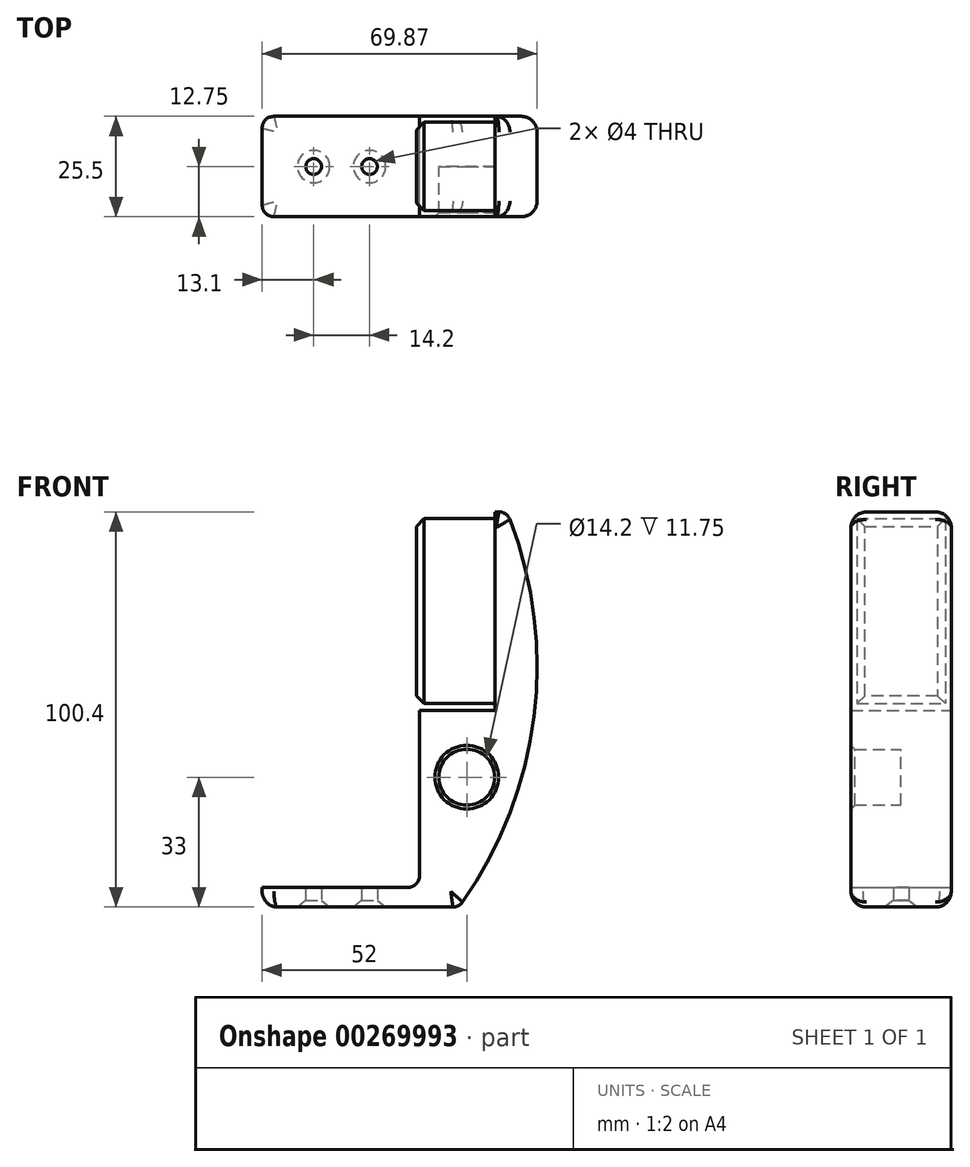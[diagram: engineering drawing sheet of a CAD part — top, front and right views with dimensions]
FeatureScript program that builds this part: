
annotation { "Feature Type Name" : "Feature", "Feature Type Description" : "" }
export const myFeature = defineFeature(function(context is Context, id is Id, definition is map)
    precondition{}
    {
        {
            var Q0;
            Q0=qCreatedBy(makeId("Front.planeOp"),FACE);
            var sketch = newSketch(context, id + "F0", { "sketchPlane" : qUnion([Q0])});
            skLineSegment(sketch, "E0.bottom", {"start": v(0, 0) * mm, "end": v(-40, 0) * mm});
            skLineSegment(sketch, "E0.top", {"start": v(0, 5) * mm, "end": v(-40, 5) * mm});
            skLineSegment(sketch, "E0.right", {"start": v(-40, 0) * mm, "end": v(-40, 5) * mm});
            skLineSegment(sketch, "E1", {"start": v(0, 5) * mm, "end": v(0, 50) * mm});
            skLineSegment(sketch, "E2", {"start": v(0, 50) * mm, "end": v(19.2, 50) * mm});
            skLineSegment(sketch, "E3", {"start": v(19.2, 50) * mm, "end": v(19.2, 51.7) * mm});
            skLineSegment(sketch, "E4", {"start": v(19.2, 51.7) * mm, "end": v(-0.8, 51.7) * mm});
            skLineSegment(sketch, "E5", {"start": v(-0.8, 51.7) * mm, "end": v(-0.8, 98.7) * mm});
            skLineSegment(sketch, "E6", {"start": v(-0.8, 98.7) * mm, "end": v(19.2, 98.7) * mm});
            skLineSegment(sketch, "E7", {"start": v(19.2, 98.7) * mm, "end": v(19.2, 100.4) * mm});
            skLineSegment(sketch, "E8", {"start": v(0, 0) * mm, "end": v(10, 0) * mm});
            skArc(sketch, "E9", {"start": v(10, 0) * mm, "mid": v(29.1, 48.62) * mm, "end": v(22.2, 100.4) * mm});
            skLineSegment(sketch, "E10", {"start": v(19.2, 100.4) * mm, "end": v(22.2, 100.4) * mm});
            skLineSegment(sketch, "E11", {"start": v(19.2, 98.7) * mm, "end": v(19.2, 51.7) * mm});
            skCircle(sketch, "E12", {"center": v(12, 33) * mm, "radius": 7.1 * mm});
            skSolve(sketch);
        }
        {
            var Q0;
            Q0=makeQuery(id+"F0.imprint","IMPRINT",FACE,{"disambiguationData":[TD([[makeQuery(id+"F0.imprint","IMPRINT",EDGE,{"derivedFrom":sQuery(id+"F0.wireOp",EDGE,"E0.bottom")}),-1.0]])]});
            extrude(context, id + "F1", {"entities" : qUnion([Q0]), "depth" : 12.75 * mm, "offsetDistance" : 25 * mm, "hasSecondDirection" : true, "secondDirectionOppositeDirection" : true, "secondDirectionDepth" : 12.75 * mm});
        }
        {
            var Q0;
            Q0=makeQuery(id+"F0.imprint","IMPRINT",FACE,{"disambiguationData":[TD([[makeQuery(id+"F0.imprint","IMPRINT",EDGE,{"derivedFrom":sQuery(id+"F0.wireOp",EDGE,"E4")}),-1.0]])]});
            extrude(context, id + "F2", {"entities" : qUnion([Q0]), "operationType" : NewBodyOperationType.ADD, "depth" : 11.25 * mm, "offsetDistance" : 25 * mm, "hasSecondDirection" : true, "secondDirectionOppositeDirection" : true, "secondDirectionDepth" : 11.25 * mm});
        }
        {
            var Q0;
            Q0=makeQuery(id+"F1.opExtrude","SWEPT_EDGE",EDGE,{"disambiguationData":[OSD([sQuery(id+"F0.wireOp",EDGE,"E0.top"),sQuery(id+"F0.wireOp",EDGE,"E1")])]});
            var Q1;
            Q1=makeQuery(id+"F1.opExtrude","CAP_EDGE",EDGE,{"disambiguationData":[OSD([sQuery(id+"F0.wireOp",EDGE,"E0.right")])],"isStart":false});
            var Q2;
            Q2=makeQuery(id+"F1.opExtrude","CAP_EDGE",EDGE,{"disambiguationData":[OSD([sQuery(id+"F0.wireOp",EDGE,"E0.right")])],"isStart":true});
            var Q3;
            Q3=makeQuery(id+"F1.opExtrude","SWEPT_EDGE",EDGE,{"disambiguationData":[OSD([sQuery(id+"F0.wireOp",EDGE,"E8"),sQuery(id+"F0.wireOp",EDGE,"E9")])]});
            var Q4;
            Q4=makeQuery(id+"F1.opExtrude","SWEPT_EDGE",EDGE,{"disambiguationData":[OSD([sQuery(id+"F0.wireOp",EDGE,"E9"),sQuery(id+"F0.wireOp",EDGE,"E10")])]});
            fillet(context, id + "F3", {"entities" : qUnion([Q0, Q1, Q2, Q3, Q4]), "tangentPropagation" : true, "radius" : 3 * mm, "defaultsChanged" : false, "vertexSettings" : [], "allowEdgeOverflow" : false});
        }
        {
            var Q0;
            Q0=makeQuery(id+"F1.opExtrude","CAP_EDGE",EDGE,{"disambiguationData":[OSD([sQuery(id+"F0.wireOp",EDGE,"E9")])],"isStart":true});
            fillet(context, id + "F4", {"entities" : qUnion([Q0]), "tangentPropagation" : true, "radius" : 4 * mm, "defaultsChanged" : true, "vertexSettings" : [], "allowEdgeOverflow" : false});
        }
        {
            var Q0;
            Q0=makeQuery(id+"F1.opExtrude","SWEPT_FACE",FACE,{"disambiguationData":[OSD([sQuery(id+"F0.wireOp",EDGE,"E0.bottom"),sQuery(id+"F0.wireOp",EDGE,"E8")])]});
            var sketch = newSketch(context, id + "F5", { "sketchPlane" : qUnion([Q0])});
            skCircle(sketch, "E13", {"center": v(-26.9, 0) * mm, "radius": 2 * mm});
            skCircle(sketch, "E14", {"center": v(-26.9, 0) * mm, "radius": 4.1 * mm});
            skCircle(sketch, "E15", {"center": v(-12.7, 0) * mm, "radius": 2 * mm});
            skCircle(sketch, "E16", {"center": v(-12.7, 0) * mm, "radius": 4.1 * mm});
            skSolve(sketch);
        }
        {
            var Q0;
            Q0=makeQuery(id+"F5.imprint","IMPRINT",FACE,{"disambiguationData":[TD([[makeQuery(id+"F5.imprint","IMPRINT",EDGE,{"derivedFrom":sQuery(id+"F5.wireOp",EDGE,"E15")}),1.0]])]});
            var Q1;
            Q1=makeQuery(id+"F5.imprint","IMPRINT",FACE,{"disambiguationData":[TD([[makeQuery(id+"F5.imprint","IMPRINT",EDGE,{"derivedFrom":sQuery(id+"F5.wireOp",EDGE,"E13")}),1.0]])]});
            var Q2;
            Q2=makeQuery(id+"F1.opExtrude","SWEPT_FACE",FACE,{"disambiguationData":[OSD([sQuery(id+"F0.wireOp",EDGE,"E0.top")])]});
            extrude(context, id + "F6", {"entities" : qUnion([Q0, Q1]), "operationType" : NewBodyOperationType.REMOVE, "endBound" : BoundingType.UP_TO_SURFACE, "oppositeDirection" : true, "depth" : 25 * mm, "endBoundEntityFace" : qUnion([Q2]), "offsetDistance" : 25 * mm});
        }
        {
            var Q0;
            Q0=makeQuery(id+"F5.imprint","IMPRINT",FACE,{"disambiguationData":[TD([[makeQuery(id+"F5.imprint","IMPRINT",EDGE,{"derivedFrom":sQuery(id+"F5.wireOp",EDGE,"E15")}),-1.0]])]});
            var Q1;
            Q1=makeQuery(id+"F5.imprint","IMPRINT",FACE,{"disambiguationData":[TD([[makeQuery(id+"F5.imprint","IMPRINT",EDGE,{"derivedFrom":sQuery(id+"F5.wireOp",EDGE,"E15")}),1.0]])]});
            var Q2;
            Q2=makeQuery(id+"F5.imprint","IMPRINT",FACE,{"disambiguationData":[TD([[makeQuery(id+"F5.imprint","IMPRINT",EDGE,{"derivedFrom":sQuery(id+"F5.wireOp",EDGE,"E13")}),-1.0]])]});
            var Q3;
            Q3=makeQuery(id+"F5.imprint","IMPRINT",FACE,{"disambiguationData":[TD([[makeQuery(id+"F5.imprint","IMPRINT",EDGE,{"derivedFrom":sQuery(id+"F5.wireOp",EDGE,"E13")}),1.0]])]});
            extrude(context, id + "F7", {"entities" : qUnion([Q0, Q1, Q2, Q3]), "operationType" : NewBodyOperationType.REMOVE, "oppositeDirection" : true, "depth" : 3 * mm, "offsetDistance" : 25 * mm, "hasDraft" : true, "draftAngle" : 50 * degree, "draftPullDirection" : true});
        }
        {
            var Q0;
            Q0=makeQuery(id+"F0.imprint","IMPRINT",FACE,{"disambiguationData":[TD([[makeQuery(id+"F0.imprint","IMPRINT",EDGE,{"derivedFrom":sQuery(id+"F0.wireOp",EDGE,"E12")}),1.0]])]});
            var Q1;
            Q1=makeQuery(id+"F1.opExtrude","CAP_FACE",FACE,{"disambiguationData":[OSD([sQuery(id+"F0.wireOp",EDGE,"E0.bottom"),sQuery(id+"F0.wireOp",EDGE,"E0.top"),sQuery(id+"F0.wireOp",EDGE,"E0.right"),sQuery(id+"F0.wireOp",EDGE,"E1"),sQuery(id+"F0.wireOp",EDGE,"E2"),sQuery(id+"F0.wireOp",EDGE,"E3"),sQuery(id+"F0.wireOp",EDGE,"E7"),sQuery(id+"F0.wireOp",EDGE,"E8"),sQuery(id+"F0.wireOp",EDGE,"E9"),sQuery(id+"F0.wireOp",EDGE,"E10"),sQuery(id+"F0.wireOp",EDGE,"E11"),sQuery(id+"F0.wireOp",EDGE,"E12")])],"isStart":true});
            extrude(context, id + "F8", {"entities" : qUnion([Q0]), "operationType" : NewBodyOperationType.ADD, "endBound" : BoundingType.UP_TO_SURFACE, "oppositeDirection" : true, "depth" : 25 * mm, "endBoundEntityFace" : qUnion([Q1]), "offsetDistance" : 25 * mm});
        }
        {
            var Q0;
            Q0=makeQuery(id+"F1.opExtrude","CAP_EDGE",EDGE,{"disambiguationData":[OSD([sQuery(id+"F0.wireOp",EDGE,"E12")])],"isStart":false});
            chamfer(context, id + "F9", {"entities" : qUnion([Q0]), "width" : 1 * mm, "tangentPropagation" : true});
        }
        {
            var Q0;
            Q0=makeQuery(id+"F2.opExtrude","SWEPT_EDGE",EDGE,{"disambiguationData":[OSD([sQuery(id+"F0.wireOp",EDGE,"E5"),sQuery(id+"F0.wireOp",EDGE,"E6")])]});
            var Q1;
            Q1=makeQuery(id+"F2.opExtrude","CAP_EDGE",EDGE,{"disambiguationData":[OSD([sQuery(id+"F0.wireOp",EDGE,"E5")])],"isStart":false});
            var Q2;
            Q2=makeQuery(id+"F2.opExtrude","CAP_EDGE",EDGE,{"disambiguationData":[OSD([sQuery(id+"F0.wireOp",EDGE,"E5")])],"isStart":true});
            var Q3;
            Q3=makeQuery(id+"F2.opExtrude","SWEPT_EDGE",EDGE,{"disambiguationData":[OSD([sQuery(id+"F0.wireOp",EDGE,"E4"),sQuery(id+"F0.wireOp",EDGE,"E5")])]});
            chamfer(context, id + "F10", {"entities" : qUnion([Q0, Q1, Q2, Q3]), "width" : 2 * mm, "tangentPropagation" : true});
        }
    });
